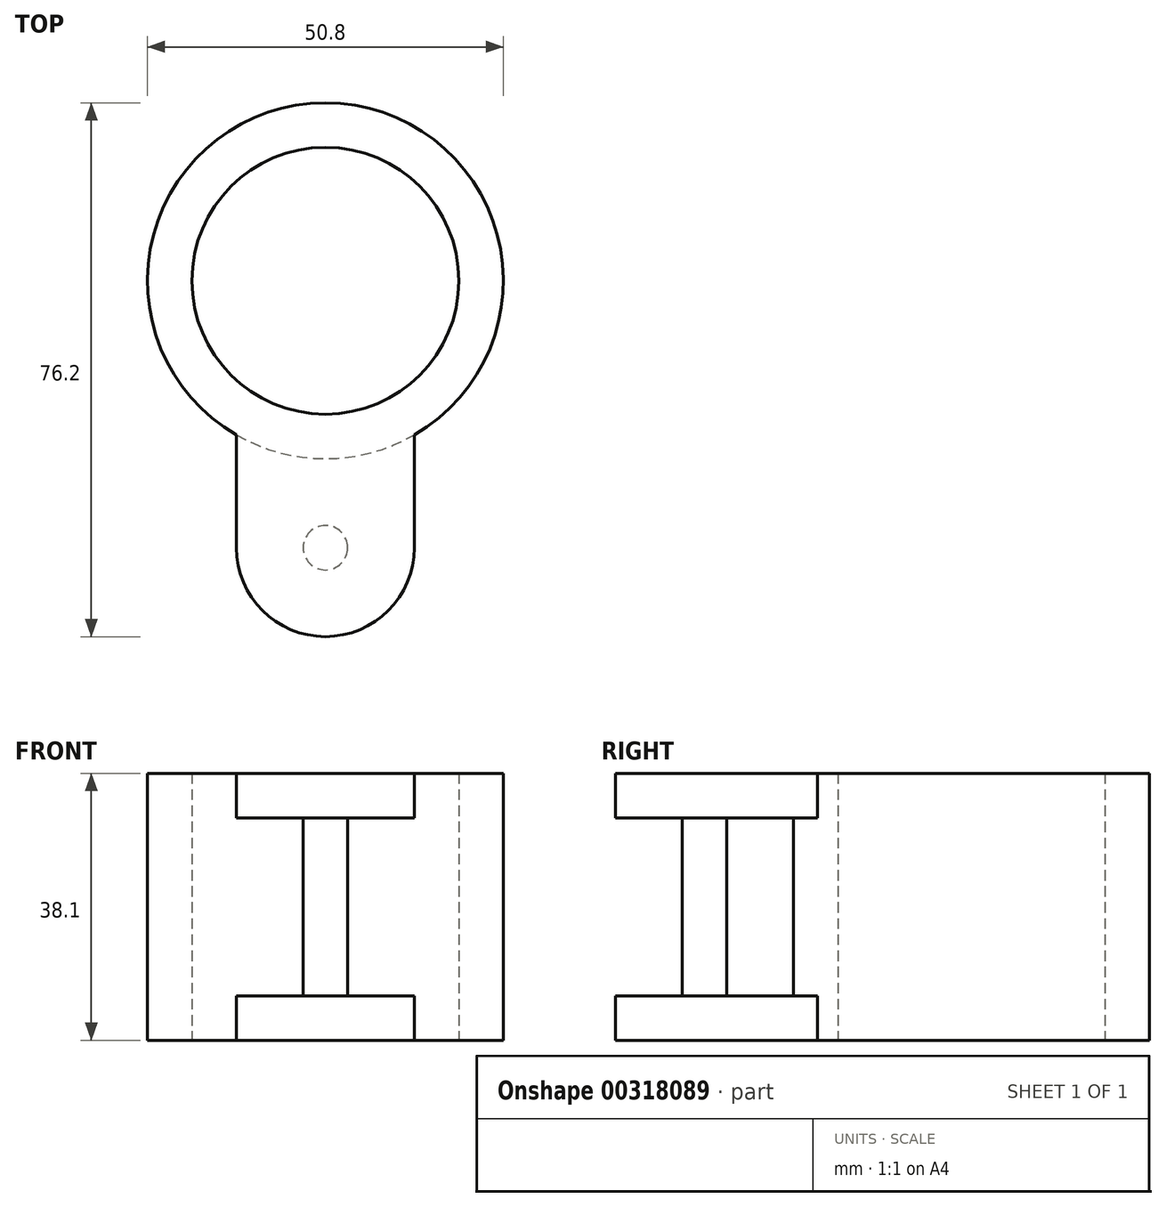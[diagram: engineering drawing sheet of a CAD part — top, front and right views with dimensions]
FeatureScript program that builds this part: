
annotation { "Feature Type Name" : "Feature", "Feature Type Description" : "" }
export const myFeature = defineFeature(function(context is Context, id is Id, definition is map)
    precondition{}
    {
        {
            var Q0;
            Q0=qCreatedBy(makeId("Top.planeOp"),FACE);
            var sketch = newSketch(context, id + "F0", { "sketchPlane" : qUnion([Q0])});
            skCircle(sketch, "E0", {"center": v(0, 0) * mm, "radius": 19.05 * mm});
            skCircle(sketch, "E1.0", {"center": v(0, 0) * mm, "radius": 25.4 * mm});
            skLineSegment(sketch, "E2", {"start": v(-12.7, -22) * mm, "end": v(-12.7, -38.1) * mm});
            skLineSegment(sketch, "E3", {"start": v(0, -50.8) * mm, "end": v(0, -50.8) * mm});
            skLineSegment(sketch, "E4", {"start": v(12.7, -38.1) * mm, "end": v(12.7, -22) * mm});
            skPoint(sketch, "E5", {"position": v(0, -50.8) * mm});
            skPoint(sketch, "E6.visualSharp", {"position": v(-12.7, -50.8) * mm});
            skArc(sketch, "E6.filletArc", {"start": v(-12.7, -38.1) * mm, "mid": v(-8.98, -47.08) * mm, "end": v(0, -50.8) * mm});
            skPoint(sketch, "E7.visualSharp", {"position": v(12.7, -50.8) * mm});
            skArc(sketch, "E7.filletArc", {"start": v(0, -50.8) * mm, "mid": v(8.98, -47.08) * mm, "end": v(12.7, -38.1) * mm});
            skSolve(sketch);
        }
        {
            var Q0;
            Q0=makeQuery(id+"F0.imprint","IMPRINT",FACE,{"disambiguationData":[TD([[makeQuery(id+"F0.imprint","IMPRINT",EDGE,{"derivedFrom":sQuery(id+"F0.wireOp",EDGE,"E0")}),-1.0]])]});
            extrude(context, id + "F1", {"entities" : qUnion([Q0]), "depth" : 38.1 * mm});
        }
        {
            var Q0;
            Q0 = qSketchRegion(id + "F0", true);
            extrude(context, id + "F2", {"entities" : qUnion([Q0]), "operationType" : NewBodyOperationType.ADD, "depth" : 6.35 * mm});
        }
        {
            var Q0;
            Q0=qCreatedBy(makeId("Top.planeOp"),FACE);
            cPlane(context, id + "F3", {"entities" : qUnion([Q0]), "cplaneType" : CPlaneType.OFFSET, "offset" : 38.1 * mm, "width" : 152.4 * mm, "height" : 152.4 * mm});
        }
        {
            var Q0;
            Q0=qCreatedBy(id+"F3.planeOp",FACE);
            var sketch = newSketch(context, id + "F4", { "sketchPlane" : qUnion([Q0])});
            skCircle(sketch, "E8.0", {"center": v(0, 0) * mm, "radius": 19.05 * mm});
            skCircle(sketch, "E8.1", {"center": v(0, 0) * mm, "radius": 25.4 * mm});
            skLineSegment(sketch, "E8.2", {"start": v(-12.7, -22) * mm, "end": v(-12.7, -38.1) * mm});
            skLineSegment(sketch, "E8.3", {"start": v(12.7, -38.1) * mm, "end": v(12.7, -22) * mm});
            skArc(sketch, "E8.4", {"start": v(-12.7, -38.1) * mm, "mid": v(-8.98, -47.08) * mm, "end": v(0, -50.8) * mm});
            skArc(sketch, "E8.5", {"start": v(0, -50.8) * mm, "mid": v(8.98, -47.08) * mm, "end": v(12.7, -38.1) * mm});
            skCircle(sketch, "E9", {"center": v(0, -38.1) * mm, "radius": 3.18 * mm});
            skSolve(sketch);
        }
        {
            var Q0;
            {var subQ1=sQuery(id+"F4.wireOp",EDGE,"E8.2");Q0=makeQuery(id+"F4.imprint","IMPRINT",FACE,{"disambiguationData":[TD([[makeQuery(id+"F4.imprint","IMPRINT",EDGE,{"derivedFrom":subQ1}),1.0]])]});}
            var Q1;
            Q1=makeQuery(id+"F4.imprint","IMPRINT",FACE,{"disambiguationData":[TD([[makeQuery(id+"F4.imprint","IMPRINT",EDGE,{"derivedFrom":sQuery(id+"F4.wireOp",EDGE,"E9")}),1.0]])]});
            extrude(context, id + "F5", {"entities" : qUnion([Q0, Q1]), "operationType" : NewBodyOperationType.ADD, "oppositeDirection" : true, "depth" : 6.35 * mm});
        }
        {
            var Q0;
            Q0=makeQuery(id+"F4.imprint","IMPRINT",FACE,{"disambiguationData":[TD([[makeQuery(id+"F4.imprint","IMPRINT",EDGE,{"derivedFrom":sQuery(id+"F4.wireOp",EDGE,"E9")}),1.0]])]});
            extrude(context, id + "F6", {"entities" : qUnion([Q0]), "operationType" : NewBodyOperationType.ADD, "oppositeDirection" : true, "depth" : 38.1 * mm});
        }
    });
